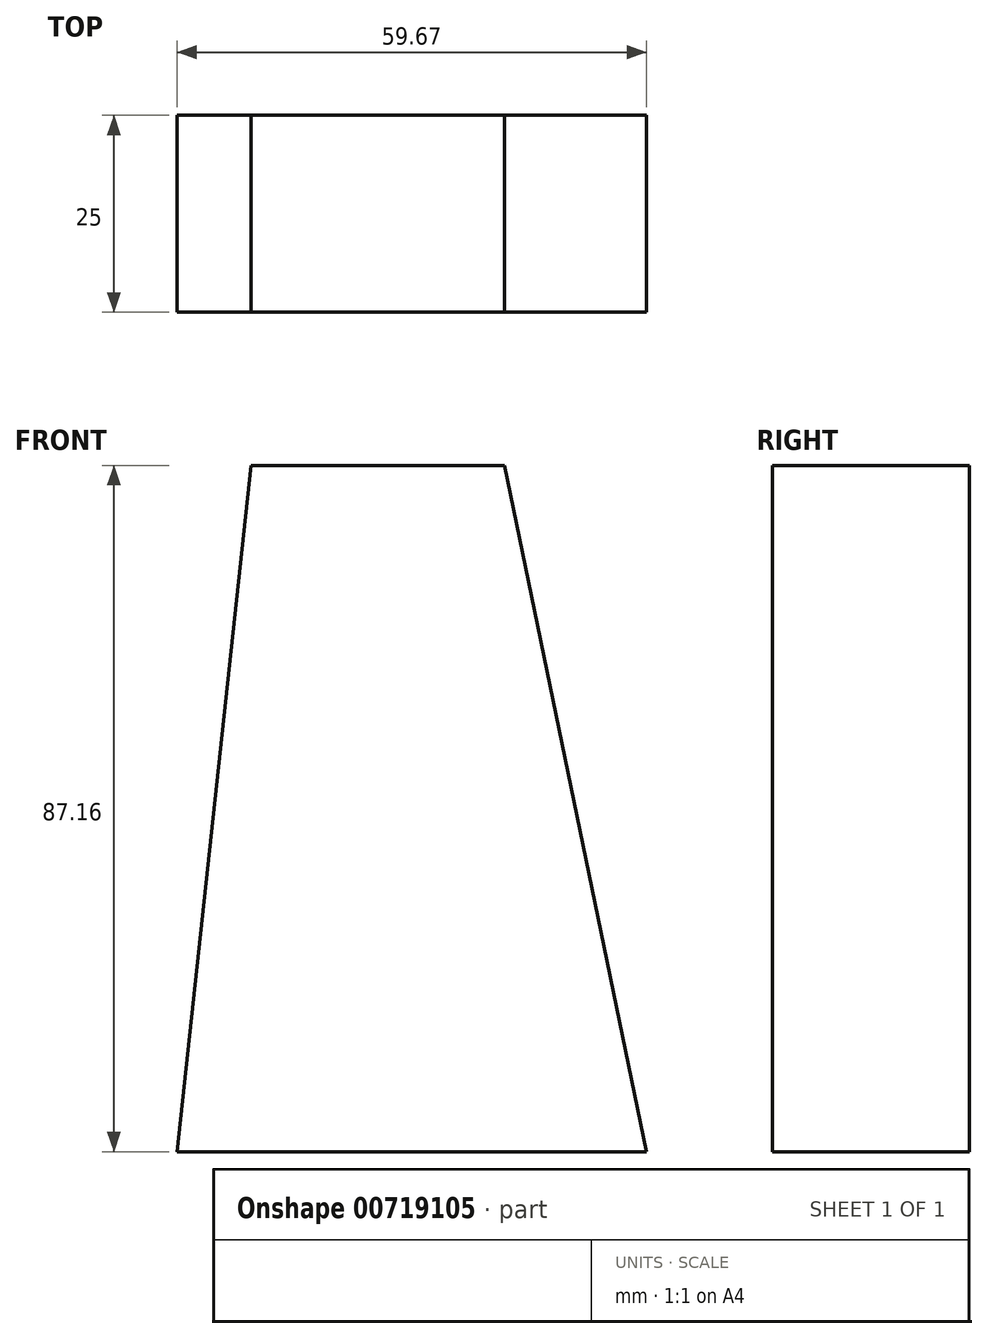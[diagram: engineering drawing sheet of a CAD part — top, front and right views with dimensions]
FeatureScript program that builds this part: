
annotation { "Feature Type Name" : "Feature", "Feature Type Description" : "" }
export const myFeature = defineFeature(function(context is Context, id is Id, definition is map)
    precondition{}
    {
        {
            var Q0;
            Q0=qCreatedBy(makeId("Front.planeOp"),FACE);
            var sketch = newSketch(context, id + "F0", { "sketchPlane" : qUnion([Q0])});
            skLineSegment(sketch, "E0", {"start": v(-28.66, -54.97) * mm, "end": v(31.01, -54.97) * mm});
            skLineSegment(sketch, "E1", {"start": v(-28.66, -54.97) * mm, "end": v(-19.26, 32.19) * mm});
            skLineSegment(sketch, "E2", {"start": v(-19.26, 32.19) * mm, "end": v(12.93, 32.19) * mm});
            skLineSegment(sketch, "E3", {"start": v(12.93, 32.19) * mm, "end": v(31.01, -54.97) * mm});
            skSolve(sketch);
        }
        {
            var Q0;
            Q0 = qSketchRegion(id + "F0", true);
            extrude(context, id + "F1", {"entities" : qUnion([Q0]), "depth" : 25 * mm, "offsetDistance" : 25 * mm});
        }
    });
